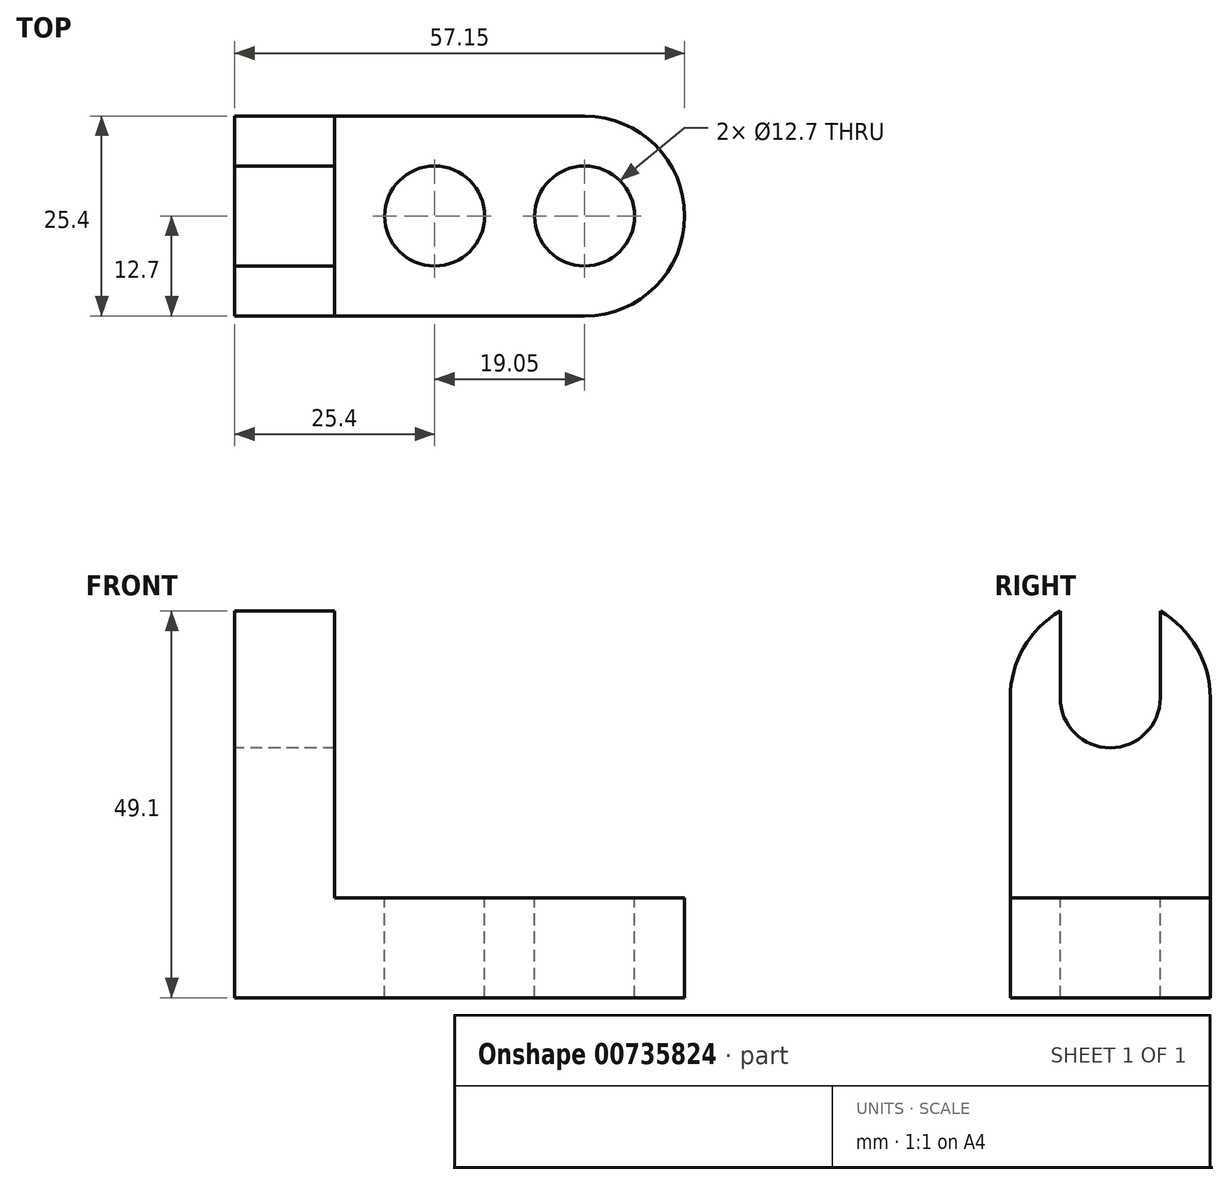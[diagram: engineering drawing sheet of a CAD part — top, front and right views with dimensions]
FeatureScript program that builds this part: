
annotation { "Feature Type Name" : "Feature", "Feature Type Description" : "" }
export const myFeature = defineFeature(function(context is Context, id is Id, definition is map)
    precondition{}
    {
        {
            var Q0;
            Q0=qCreatedBy(makeId("Top.planeOp"),FACE);
            var sketch = newSketch(context, id + "F0", { "sketchPlane" : qUnion([Q0])});
            skLineSegment(sketch, "E0.bottom", {"start": v(0, 0) * mm, "end": v(44.45, 0) * mm});
            skLineSegment(sketch, "E0.top", {"start": v(0, 25.4) * mm, "end": v(44.45, 25.4) * mm});
            skLineSegment(sketch, "E0.left", {"start": v(0, 0) * mm, "end": v(0, 25.4) * mm});
            skLineSegment(sketch, "E0.right", {"start": v(44.45, 0) * mm, "end": v(44.45, 25.4) * mm});
            skSolve(sketch);
        }
        {
            var Q0;
            Q0 = qSketchRegion(id + "F0", true);
            extrude(context, id + "F1", {"entities" : qUnion([Q0]), "depth" : 12.7 * mm, "offsetDistance" : 25.4 * mm});
        }
        {
            var Q0;
            Q0=makeQuery(id+"F1.opExtrude","CAP_FACE",FACE,{"disambiguationData":[OSD([sQuery(id+"F0.wireOp",EDGE,"E0.bottom"),sQuery(id+"F0.wireOp",EDGE,"E0.top"),sQuery(id+"F0.wireOp",EDGE,"E0.left"),sQuery(id+"F0.wireOp",EDGE,"E0.right")])],"isStart":false});
            var sketch = newSketch(context, id + "F2", { "sketchPlane" : qUnion([Q0])});
            skCircle(sketch, "E1", {"center": v(44.45, 12.7) * mm, "radius": 12.7 * mm});
            skSolve(sketch);
        }
        {
            var Q0;
            Q0 = qSketchRegion(id + "F2", true);
            extrude(context, id + "F3", {"entities" : qUnion([Q0]), "operationType" : NewBodyOperationType.ADD, "oppositeDirection" : true, "depth" : 12.7 * mm, "offsetDistance" : 25.4 * mm});
        }
        {
            var Q0;
            Q0=makeQuery(id+"F3.boolean.opBoolean","MERGE",FACE,{"derivedFrom":[makeQuery(id+"F1.opExtrude","CAP_FACE",FACE,{"disambiguationData":[OSD([sQuery(id+"F0.wireOp",EDGE,"E0.bottom"),sQuery(id+"F0.wireOp",EDGE,"E0.top"),sQuery(id+"F0.wireOp",EDGE,"E0.left"),sQuery(id+"F0.wireOp",EDGE,"E0.right")])],"isStart":false}),makeQuery(id+"F3.opExtrude","CAP_FACE",FACE,{"disambiguationData":[OSD([sQuery(id+"F2.wireOp",EDGE,"E1")])],"isStart":true})]});
            var sketch = newSketch(context, id + "F4", { "sketchPlane" : qUnion([Q0])});
            skLineSegment(sketch, "E2", {"start": v(0, 0) * mm, "end": v(0, 25.4) * mm});
            skLineSegment(sketch, "E3", {"start": v(0, 25.4) * mm, "end": v(12.7, 25.4) * mm});
            skLineSegment(sketch, "E4", {"start": v(12.7, 25.4) * mm, "end": v(12.7, 0) * mm});
            skLineSegment(sketch, "E5", {"start": v(12.7, 0) * mm, "end": v(0, 0) * mm});
            skSolve(sketch);
        }
        {
            var Q0;
            Q0 = qSketchRegion(id + "F4", true);
            extrude(context, id + "F5", {"entities" : qUnion([Q0]), "operationType" : NewBodyOperationType.ADD, "depth" : 25.4 * mm, "offsetDistance" : 25.4 * mm});
        }
        {
            var Q0;
            Q0=makeQuery(id+"F5.boolean.opBoolean","MERGE",FACE,{"derivedFrom":[makeQuery(id+"F1.opExtrude","SWEPT_FACE",FACE,{"disambiguationData":[OSD([sQuery(id+"F0.wireOp",EDGE,"E0.left")])]}),makeQuery(id+"F5.opExtrude","SWEPT_FACE",FACE,{"disambiguationData":[OSD([sQuery(id+"F4.wireOp",EDGE,"E2")])]})]});
            var sketch = newSketch(context, id + "F6", { "sketchPlane" : qUnion([Q0])});
            skCircle(sketch, "E6", {"center": v(-12.7, 38.1) * mm, "radius": 12.7 * mm});
            skSolve(sketch);
        }
        {
            var Q0;
            Q0 = qSketchRegion(id + "F6", true);
            extrude(context, id + "F7", {"entities" : qUnion([Q0]), "operationType" : NewBodyOperationType.ADD, "oppositeDirection" : true, "depth" : 12.7 * mm, "offsetDistance" : 25.4 * mm});
        }
        {
            var Q0;
            Q0=makeQuery(id+"F7.boolean.opBoolean","MERGE",FACE,{"derivedFrom":[makeQuery(id+"F5.boolean.opBoolean","MERGE",FACE,{"derivedFrom":[makeQuery(id+"F1.opExtrude","SWEPT_FACE",FACE,{"disambiguationData":[OSD([sQuery(id+"F0.wireOp",EDGE,"E0.left")])]}),makeQuery(id+"F5.opExtrude","SWEPT_FACE",FACE,{"disambiguationData":[OSD([sQuery(id+"F4.wireOp",EDGE,"E2")])]})]}),makeQuery(id+"F7.opExtrude","CAP_FACE",FACE,{"disambiguationData":[OSD([sQuery(id+"F6.wireOp",EDGE,"E6")])],"isStart":true})]});
            var sketch = newSketch(context, id + "F8", { "sketchPlane" : qUnion([Q0])});
            skCircle(sketch, "E7", {"center": v(-12.7, 38.1) * mm, "radius": 6.35 * mm});
            skSolve(sketch);
        }
        {
            var Q0;
            Q0 = qSketchRegion(id + "F8", true);
            extrude(context, id + "F9", {"entities" : qUnion([Q0]), "operationType" : NewBodyOperationType.REMOVE, "oppositeDirection" : true, "depth" : 12.7 * mm, "offsetDistance" : 25.4 * mm});
        }
        {
            var Q0;
            Q0=makeQuery(id+"F7.boolean.opBoolean","MERGE",FACE,{"derivedFrom":[makeQuery(id+"F5.opExtrude","SWEPT_FACE",FACE,{"disambiguationData":[OSD([sQuery(id+"F4.wireOp",EDGE,"E4")])]}),makeQuery(id+"F7.opExtrude","CAP_FACE",FACE,{"disambiguationData":[OSD([sQuery(id+"F6.wireOp",EDGE,"E6")])],"isStart":false})]});
            var sketch = newSketch(context, id + "F10", { "sketchPlane" : qUnion([Q0])});
            skLineSegment(sketch, "E8", {"start": v(19.05, 38.1) * mm, "end": v(19.05, 59.39) * mm});
            skLineSegment(sketch, "E9", {"start": v(19.05, 59.39) * mm, "end": v(6.35, 59.39) * mm});
            skLineSegment(sketch, "E10", {"start": v(6.35, 59.39) * mm, "end": v(6.35, 38.1) * mm});
            skLineSegment(sketch, "E11", {"start": v(6.35, 38.1) * mm, "end": v(19.05, 38.1) * mm});
            skSolve(sketch);
        }
        {
            var Q0;
            Q0 = qSketchRegion(id + "F10", true);
            extrude(context, id + "F11", {"entities" : qUnion([Q0]), "operationType" : NewBodyOperationType.REMOVE, "oppositeDirection" : true, "depth" : 25.4 * mm, "offsetDistance" : 25.4 * mm});
        }
        {
            var Q0;
            Q0=makeQuery(id+"F3.boolean.opBoolean","MERGE",FACE,{"derivedFrom":[makeQuery(id+"F1.opExtrude","CAP_FACE",FACE,{"disambiguationData":[OSD([sQuery(id+"F0.wireOp",EDGE,"E0.bottom"),sQuery(id+"F0.wireOp",EDGE,"E0.top"),sQuery(id+"F0.wireOp",EDGE,"E0.left"),sQuery(id+"F0.wireOp",EDGE,"E0.right")])],"isStart":false}),makeQuery(id+"F3.opExtrude","CAP_FACE",FACE,{"disambiguationData":[OSD([sQuery(id+"F2.wireOp",EDGE,"E1")])],"isStart":true})]});
            var sketch = newSketch(context, id + "F12", { "sketchPlane" : qUnion([Q0])});
            skCircle(sketch, "E12", {"center": v(44.45, 12.7) * mm, "radius": 6.35 * mm});
            skCircle(sketch, "E13", {"center": v(25.4, 12.7) * mm, "radius": 6.35 * mm});
            skSolve(sketch);
        }
        {
            var Q0;
            Q0 = qSketchRegion(id + "F12", true);
            extrude(context, id + "F13", {"entities" : qUnion([Q0]), "operationType" : NewBodyOperationType.REMOVE, "oppositeDirection" : true, "depth" : 25.4 * mm, "offsetDistance" : 25.4 * mm});
        }
    });
